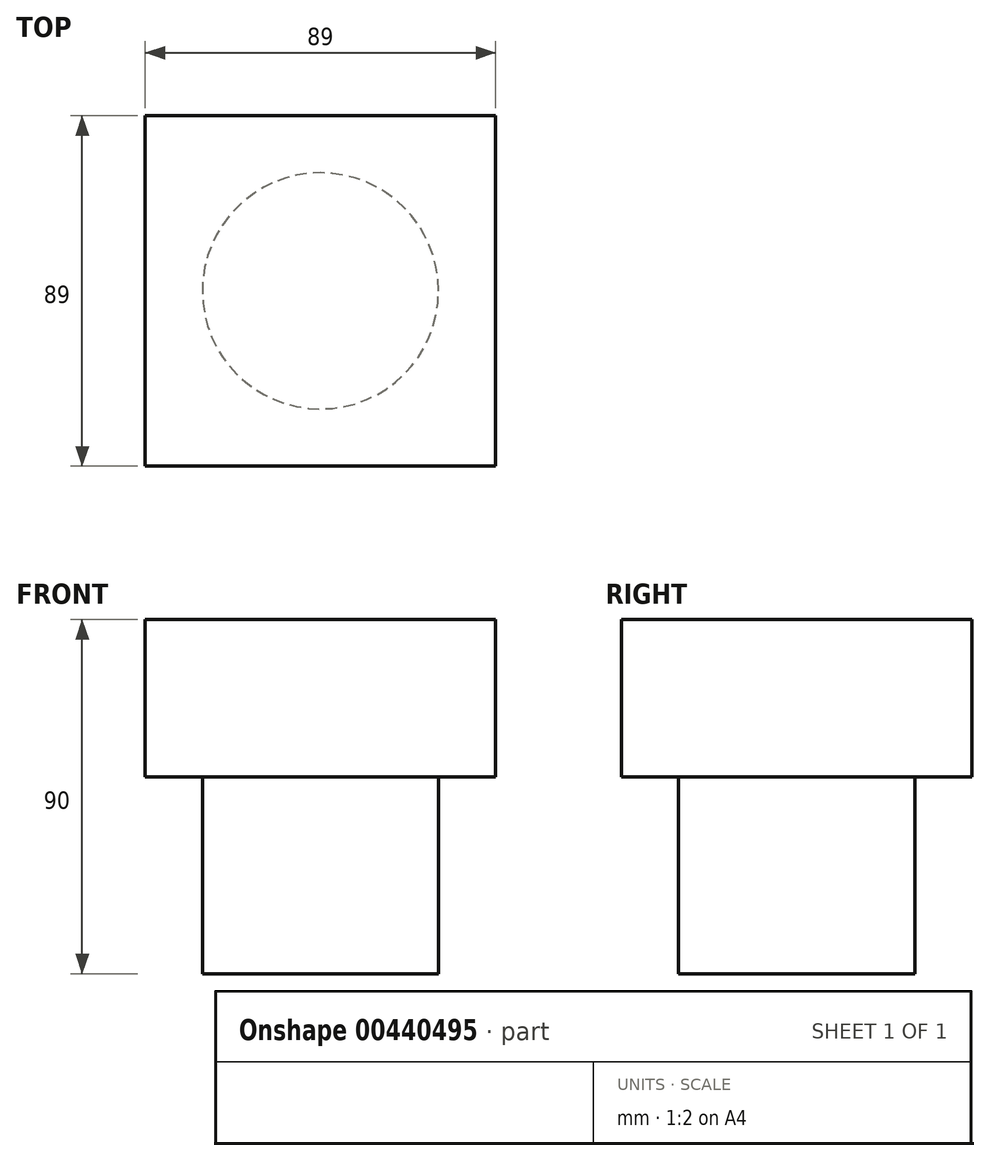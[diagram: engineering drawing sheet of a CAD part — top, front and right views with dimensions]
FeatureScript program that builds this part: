
annotation { "Feature Type Name" : "Feature", "Feature Type Description" : "" }
export const myFeature = defineFeature(function(context is Context, id is Id, definition is map)
    precondition{}
    {
        {
            var Q0;
            Q0=qCreatedBy(makeId("Top.planeOp"),FACE);
            var sketch = newSketch(context, id + "F0", { "sketchPlane" : qUnion([Q0])});
            skLineSegment(sketch, "E0.bottom", {"start": v(44.5, 44.5) * mm, "end": v(-44.5, 44.5) * mm});
            skLineSegment(sketch, "E0.top", {"start": v(44.5, -44.5) * mm, "end": v(-44.5, -44.5) * mm});
            skLineSegment(sketch, "E0.left", {"start": v(44.5, 44.5) * mm, "end": v(44.5, -44.5) * mm});
            skLineSegment(sketch, "E0.right", {"start": v(-44.5, 44.5) * mm, "end": v(-44.5, -44.5) * mm});
            skPoint(sketch, "E0.middle", {"position": v(0, 0) * mm});
            skSolve(sketch);
        }
        {
            var Q0;
            Q0 = qSketchRegion(id + "F0", true);
            extrude(context, id + "F1", {"entities" : qUnion([Q0]), "offsetDistance" : 25 * mm, "depth" : 40 * mm});
        }
        {
            var Q0;
            Q0=makeQuery(id+"F1.opExtrude","CAP_FACE",FACE,{"disambiguationData":[OSD([sQuery(id+"F0.wireOp",EDGE,"E0.bottom"),sQuery(id+"F0.wireOp",EDGE,"E0.top"),sQuery(id+"F0.wireOp",EDGE,"E0.left"),sQuery(id+"F0.wireOp",EDGE,"E0.right")])],"isStart":true});
            var sketch = newSketch(context, id + "F2", { "sketchPlane" : qUnion([Q0])});
            skCircle(sketch, "E1", {"center": v(0, 0) * mm, "radius": 30 * mm});
            skSolve(sketch);
        }
        {
            var Q0;
            Q0 = qSketchRegion(id + "F2", true);
            extrude(context, id + "F3", {"entities" : qUnion([Q0]), "operationType" : NewBodyOperationType.ADD, "offsetDistance" : 25 * mm, "depth" : 50 * mm});
        }
    });
